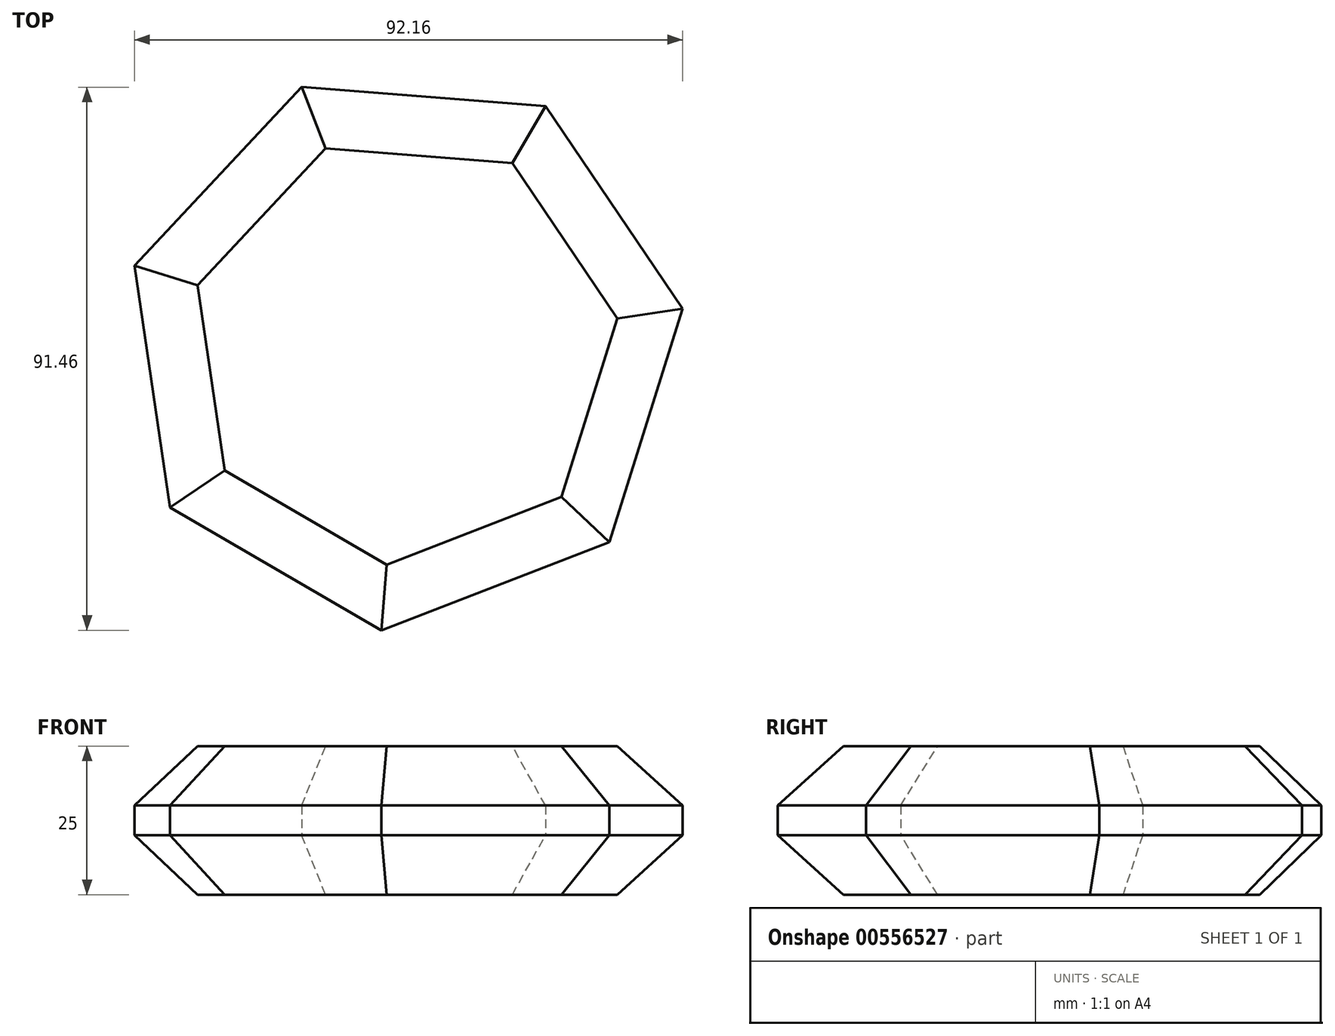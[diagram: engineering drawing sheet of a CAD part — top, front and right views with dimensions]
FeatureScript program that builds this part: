
annotation { "Feature Type Name" : "Feature", "Feature Type Description" : "" }
export const myFeature = defineFeature(function(context is Context, id is Id, definition is map)
    precondition{}
    {
        {
            var Q0;
            Q0=qCreatedBy(makeId("Top.planeOp"),FACE);
            var sketch = newSketch(context, id + "F0", { "sketchPlane" : qUnion([Q0])});
            skCircle(sketch, "E0.cCircle", {"center": v(2.1, 0) * mm, "radius": 42.72 * mm, "construction": true});
            skLineSegment(sketch, "E0.0", {"start": v(-1.64, -47.26) * mm, "end": v(-37.19, -26.55) * mm});
            skLineSegment(sketch, "E0.1", {"start": v(-37.19, -26.55) * mm, "end": v(-43.16, 14.15) * mm});
            skLineSegment(sketch, "E0.2", {"start": v(-43.16, 14.15) * mm, "end": v(-15.06, 44.2) * mm});
            skLineSegment(sketch, "E0.3", {"start": v(-15.06, 44.2) * mm, "end": v(25.96, 40.97) * mm});
            skLineSegment(sketch, "E0.4", {"start": v(25.96, 40.97) * mm, "end": v(49, 6.88) * mm});
            skLineSegment(sketch, "E0.5", {"start": v(49, 6.88) * mm, "end": v(36.72, -32.38) * mm});
            skLineSegment(sketch, "E0.6", {"start": v(36.72, -32.38) * mm, "end": v(-1.64, -47.26) * mm});
            skPoint(sketch, "E0.0.midPoint", {"position": v(-19.41, -36.9) * mm});
            skSolve(sketch);
        }
        {
            var Q0;
            Q0 = qSketchRegion(id + "F0", true);
            extrude(context, id + "F1", {"entities" : qUnion([Q0]), "depth" : 25 * mm, "offsetDistance" : 25 * mm});
        }
        {
            var Q0;
            Q0=makeQuery(id+"F1.opExtrude","CAP_EDGE",EDGE,{"disambiguationData":[OSD([sQuery(id+"F0.wireOp",EDGE,"E0.0")])],"isStart":false});
            var Q1;
            Q1=makeQuery(id+"F1.opExtrude","CAP_FACE",FACE,{"disambiguationData":[OSD([sQuery(id+"F0.wireOp",EDGE,"E0.0"),sQuery(id+"F0.wireOp",EDGE,"E0.1"),sQuery(id+"F0.wireOp",EDGE,"E0.2"),sQuery(id+"F0.wireOp",EDGE,"E0.3"),sQuery(id+"F0.wireOp",EDGE,"E0.4"),sQuery(id+"F0.wireOp",EDGE,"E0.5"),sQuery(id+"F0.wireOp",EDGE,"E0.6")])],"isStart":false});
            chamfer(context, id + "F2", {"entities" : qUnion([Q0, Q1]), "width" : 10 * mm, "tangentPropagation" : true});
        }
        {
            var Q0;
            Q0=makeQuery(id+"F1.opExtrude","CAP_EDGE",EDGE,{"disambiguationData":[OSD([sQuery(id+"F0.wireOp",EDGE,"E0.2")])],"isStart":true});
            var Q1;
            Q1=makeQuery(id+"F1.opExtrude","CAP_FACE",FACE,{"disambiguationData":[OSD([sQuery(id+"F0.wireOp",EDGE,"E0.0"),sQuery(id+"F0.wireOp",EDGE,"E0.1"),sQuery(id+"F0.wireOp",EDGE,"E0.2"),sQuery(id+"F0.wireOp",EDGE,"E0.3"),sQuery(id+"F0.wireOp",EDGE,"E0.4"),sQuery(id+"F0.wireOp",EDGE,"E0.5"),sQuery(id+"F0.wireOp",EDGE,"E0.6")])],"isStart":true});
            chamfer(context, id + "F3", {"entities" : qUnion([Q0, Q1]), "width" : 10 * mm, "tangentPropagation" : true});
        }
    });
